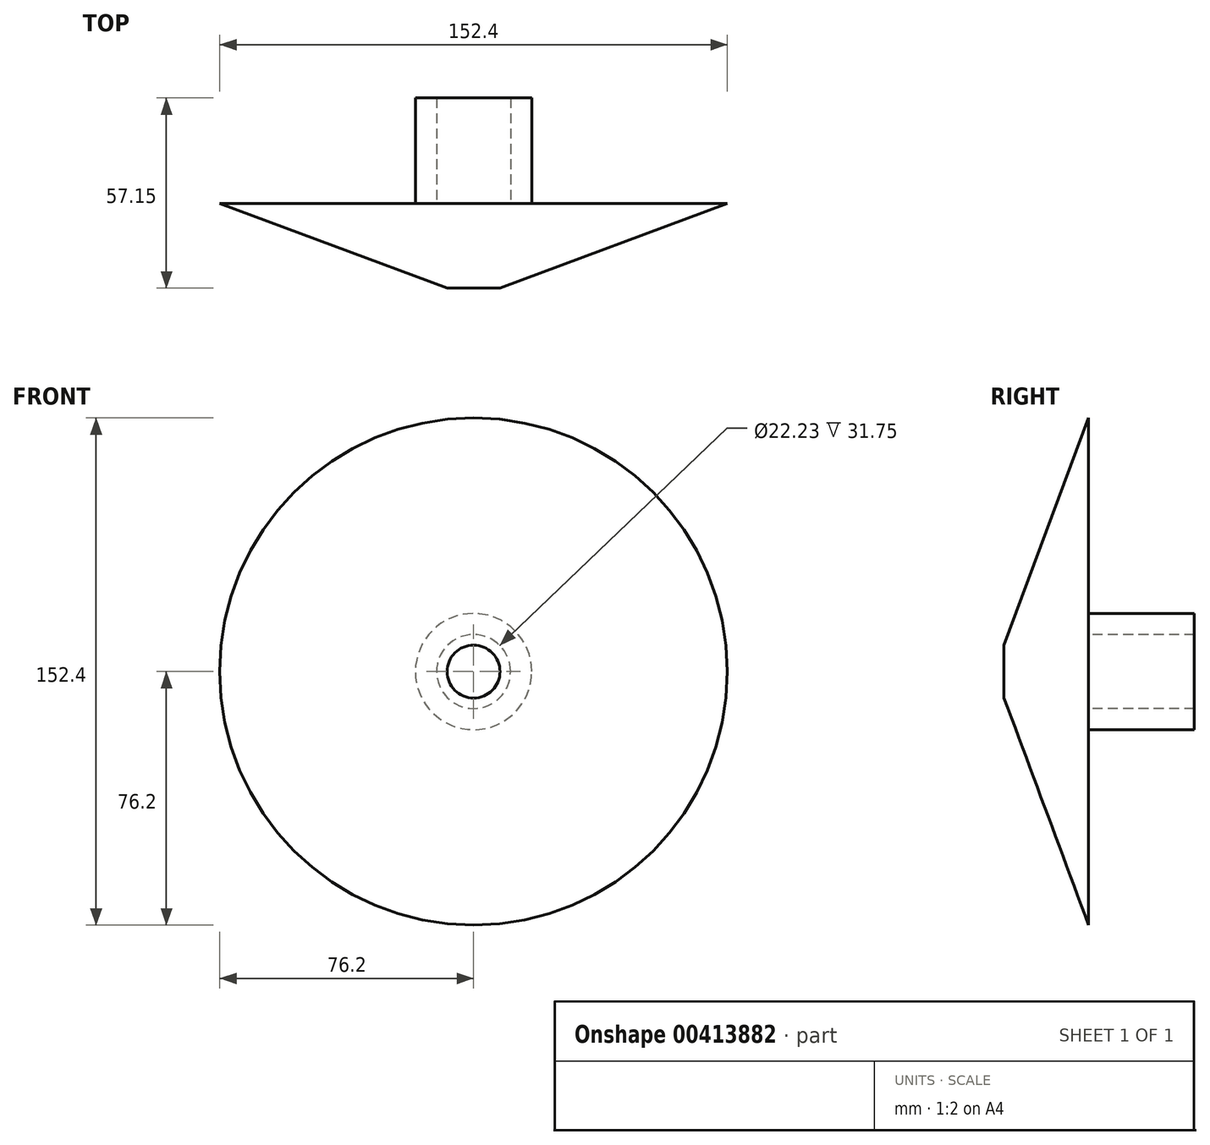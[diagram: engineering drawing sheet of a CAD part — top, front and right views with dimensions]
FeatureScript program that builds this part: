
annotation { "Feature Type Name" : "Feature", "Feature Type Description" : "" }
export const myFeature = defineFeature(function(context is Context, id is Id, definition is map)
    precondition{}
    {
        {
            var Q0;
            Q0=qCreatedBy(makeId("Front.planeOp"),FACE);
            var sketch = newSketch(context, id + "F0", { "sketchPlane" : qUnion([Q0])});
            skCircle(sketch, "E0", {"center": v(0, 0) * mm, "radius": 76.2 * mm});
            skSolve(sketch);
        }
        {
            var Q0;
            Q0=makeQuery(id+"F0.imprint","IMPRINT",FACE,{"disambiguationData":[TD([[makeQuery(id+"F0.imprint","IMPRINT",EDGE,{"derivedFrom":sQuery(id+"F0.wireOp",EDGE,"E0")}),1.0]])]});
            cPlane(context, id + "F1", {"entities" : qUnion([Q0]), "cplaneType" : CPlaneType.OFFSET, "offset" : 25.4 * mm, "width" : 152.4 * mm, "height" : 152.4 * mm});
        }
        {
            var Q0;
            Q0=qCreatedBy(id+"F1.planeOp",FACE);
            var sketch = newSketch(context, id + "F2", { "sketchPlane" : qUnion([Q0])});
            skCircle(sketch, "E1", {"center": v(0, 0) * mm, "radius": 7.94 * mm});
            skSolve(sketch);
        }
        {
            var Q0;
            Q0=makeQuery(id+"F0.imprint","IMPRINT",FACE,{"disambiguationData":[TD([[makeQuery(id+"F0.imprint","IMPRINT",EDGE,{"derivedFrom":sQuery(id+"F0.wireOp",EDGE,"E0")}),1.0]])]});
            var Q1;
            Q1=makeQuery(id+"F2.imprint","IMPRINT",FACE,{"disambiguationData":[TD([[makeQuery(id+"F2.imprint","IMPRINT",EDGE,{"derivedFrom":sQuery(id+"F2.wireOp",EDGE,"E1")}),1.0]])]});
            loft(context, id + "F3", {"sheetProfilesArray" : [{ "sheetProfileEntities" : qUnion([Q0]) }, { "sheetProfileEntities" : qUnion([Q1]) }]});
        }
        {
            var Q0;
            Q0=makeQuery(id+"F3.opLoft","CAP_FACE",FACE,{"disambiguationData":[OSD([makeQuery(id+"F0.imprint","IMPRINT",FACE,{"disambiguationData":[TD([[makeQuery(id+"F0.imprint","IMPRINT",EDGE,{"derivedFrom":sQuery(id+"F0.wireOp",EDGE,"E0")}),1.0]])]})])],"isStart":true});
            var sketch = newSketch(context, id + "F4", { "sketchPlane" : qUnion([Q0])});
            skCircle(sketch, "E2", {"center": v(0, 0) * mm, "radius": 17.46 * mm});
            skCircle(sketch, "E3", {"center": v(0, 0) * mm, "radius": 11.11 * mm});
            skSolve(sketch);
        }
        {
            var Q0;
            Q0 = qSketchRegion(id + "F4", true);
            extrude(context, id + "F5", {"entities" : qUnion([Q0]), "operationType" : NewBodyOperationType.ADD, "depth" : 31.75 * mm});
        }
    });
